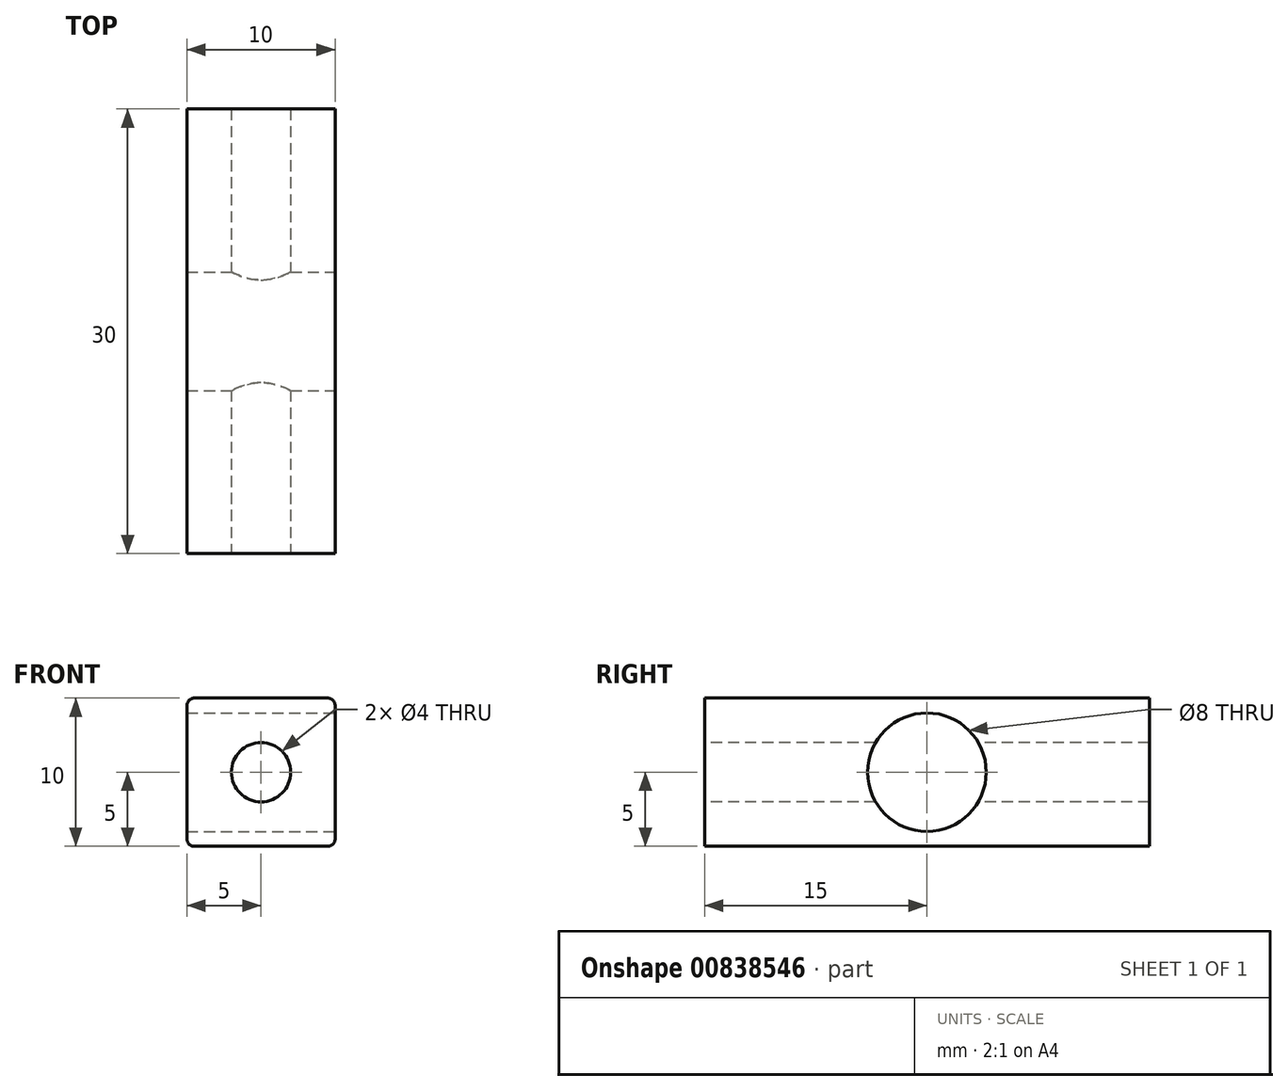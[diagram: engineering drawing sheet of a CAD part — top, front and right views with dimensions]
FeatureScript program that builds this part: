
annotation { "Feature Type Name" : "Feature", "Feature Type Description" : "" }
export const myFeature = defineFeature(function(context is Context, id is Id, definition is map)
    precondition{}
    {
        {
            var Q0;
            Q0=qCreatedBy(makeId("Front.planeOp"),FACE);
            var sketch = newSketch(context, id + "F0", { "sketchPlane" : qUnion([Q0])});
            skLineSegment(sketch, "E0.bottom", {"start": v(5, 5) * mm, "end": v(-5, 5) * mm});
            skLineSegment(sketch, "E0.top", {"start": v(5, -5) * mm, "end": v(-5, -5) * mm});
            skLineSegment(sketch, "E0.left", {"start": v(5, 5) * mm, "end": v(5, -5) * mm});
            skLineSegment(sketch, "E0.right", {"start": v(-5, 5) * mm, "end": v(-5, -5) * mm});
            skPoint(sketch, "E0.middle", {"position": v(0, 0) * mm});
            skSolve(sketch);
        }
        {
            var Q0;
            Q0 = qSketchRegion(id + "F0", true);
            extrude(context, id + "F1", {"entities" : qUnion([Q0]), "depth" : 30 * mm, "offsetDistance" : 25 * mm});
        }
        {
            var Q0;
            Q0=makeQuery(id+"F1.opExtrude","CAP_FACE",FACE,{"disambiguationData":[OSD([sQuery(id+"F0.wireOp",EDGE,"E0.bottom"),sQuery(id+"F0.wireOp",EDGE,"E0.top"),sQuery(id+"F0.wireOp",EDGE,"E0.left"),sQuery(id+"F0.wireOp",EDGE,"E0.right")])],"isStart":false});
            var sketch = newSketch(context, id + "F2", { "sketchPlane" : qUnion([Q0])});
            skCircle(sketch, "E1", {"center": v(0, 0) * mm, "radius": 2 * mm});
            skSolve(sketch);
        }
        {
            var Q0;
            Q0=makeQuery(id+"F2.imprint","IMPRINT",FACE,{"disambiguationData":[TD([[makeQuery(id+"F2.imprint","IMPRINT",EDGE,{"derivedFrom":sQuery(id+"F2.wireOp",EDGE,"E1")}),1.0]])]});
            extrude(context, id + "F3", {"entities" : qUnion([Q0]), "operationType" : NewBodyOperationType.REMOVE, "oppositeDirection" : true, "depth" : 46.4 * mm, "offsetDistance" : 25 * mm});
        }
        {
            var Q0;
            Q0=makeQuery(id+"F1.opExtrude","SWEPT_FACE",FACE,{"disambiguationData":[OSD([sQuery(id+"F0.wireOp",EDGE,"E0.left")])]});
            var sketch = newSketch(context, id + "F4", { "sketchPlane" : qUnion([Q0])});
            skCircle(sketch, "E2", {"center": v(-15, 0) * mm, "radius": 4 * mm});
            skLineSegment(sketch, "E3", {"start": v(-30, 0) * mm, "end": v(0, 0) * mm, "construction": true});
            skSolve(sketch);
        }
        {
            var Q0;
            Q0 = qSketchRegion(id + "F4", true);
            extrude(context, id + "F5", {"entities" : qUnion([Q0]), "operationType" : NewBodyOperationType.REMOVE, "oppositeDirection" : true, "depth" : 25 * mm, "offsetDistance" : 25 * mm});
        }
        {
            var Q0;
            Q0=makeQuery(id+"F1.opExtrude","SWEPT_EDGE",EDGE,{"disambiguationData":[OSD([sQuery(id+"F0.wireOp",EDGE,"E0.bottom"),sQuery(id+"F0.wireOp",EDGE,"E0.right")])]});
            var Q1;
            Q1=makeQuery(id+"F1.opExtrude","SWEPT_EDGE",EDGE,{"disambiguationData":[OSD([sQuery(id+"F0.wireOp",EDGE,"E0.top"),sQuery(id+"F0.wireOp",EDGE,"E0.left")])]});
            var Q2;
            Q2=makeQuery(id+"F1.opExtrude","SWEPT_EDGE",EDGE,{"disambiguationData":[OSD([sQuery(id+"F0.wireOp",EDGE,"E0.bottom"),sQuery(id+"F0.wireOp",EDGE,"E0.left")])]});
            var Q3;
            Q3=makeQuery(id+"F1.opExtrude","SWEPT_EDGE",EDGE,{"disambiguationData":[OSD([sQuery(id+"F0.wireOp",EDGE,"E0.top"),sQuery(id+"F0.wireOp",EDGE,"E0.right")])]});
            fillet(context, id + "F6", {"entities" : qUnion([Q0, Q1, Q2, Q3]), "radius" : 0.5 * mm, "tangentPropagation" : true, "allowEdgeOverflow" : false});
        }
    });
